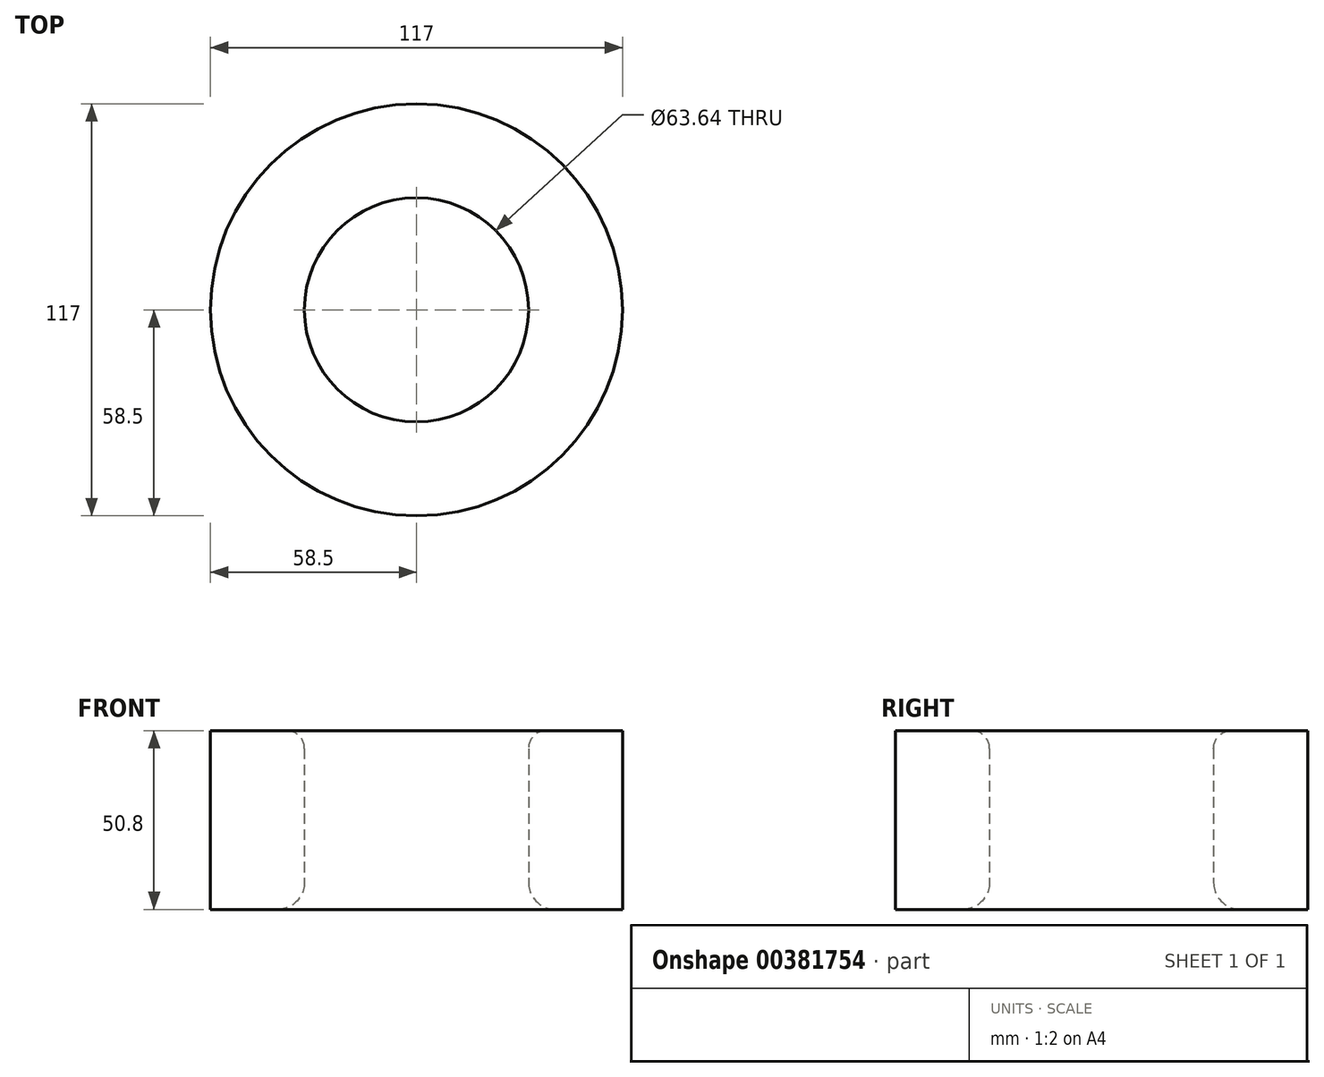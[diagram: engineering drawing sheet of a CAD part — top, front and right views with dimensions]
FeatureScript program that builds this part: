
annotation { "Feature Type Name" : "Feature", "Feature Type Description" : "" }
export const myFeature = defineFeature(function(context is Context, id is Id, definition is map)
    precondition{}
    {
        {
            var Q0;
            Q0=qCreatedBy(makeId("Top.planeOp"),FACE);
            var sketch = newSketch(context, id + "F0", { "sketchPlane" : qUnion([Q0])});
            skPoint(sketch, "E0", {"position": v(0, 0) * mm});
            skCircle(sketch, "E1", {"center": v(0, 0) * mm, "radius": 31.82 * mm});
            skCircle(sketch, "E2", {"center": v(0, 0) * mm, "radius": 58.5 * mm});
            skSolve(sketch);
        }
        {
            var Q0;
            Q0=qSketchRegion(id+"F0",true);
            extrude(context, id + "F1", {"entities" : qUnion([Q0]), "depth" : 50.8 * mm});
        }
        {
            var Q0;
            Q0=makeQuery(id+"F1.opExtrude","CAP_EDGE",EDGE,{"disambiguationData":[OSD([sQuery(id+"F0.wireOp",EDGE,"E1")])],"isStart":false});
            fillet(context, id + "F2", {"entities" : qUnion([Q0]), "radius" : 5.08 * mm, "tangentPropagation" : true, "allowEdgeOverflow" : false});
        }
        {
            var Q0;
            Q0=makeQuery(id+"F1.opExtrude","CAP_EDGE",EDGE,{"disambiguationData":[OSD([sQuery(id+"F0.wireOp",EDGE,"E1")])],"isStart":true});
            fillet(context, id + "F3", {"entities" : qUnion([Q0]), "radius" : 7.62 * mm, "tangentPropagation" : true, "allowEdgeOverflow" : false});
        }
    });
